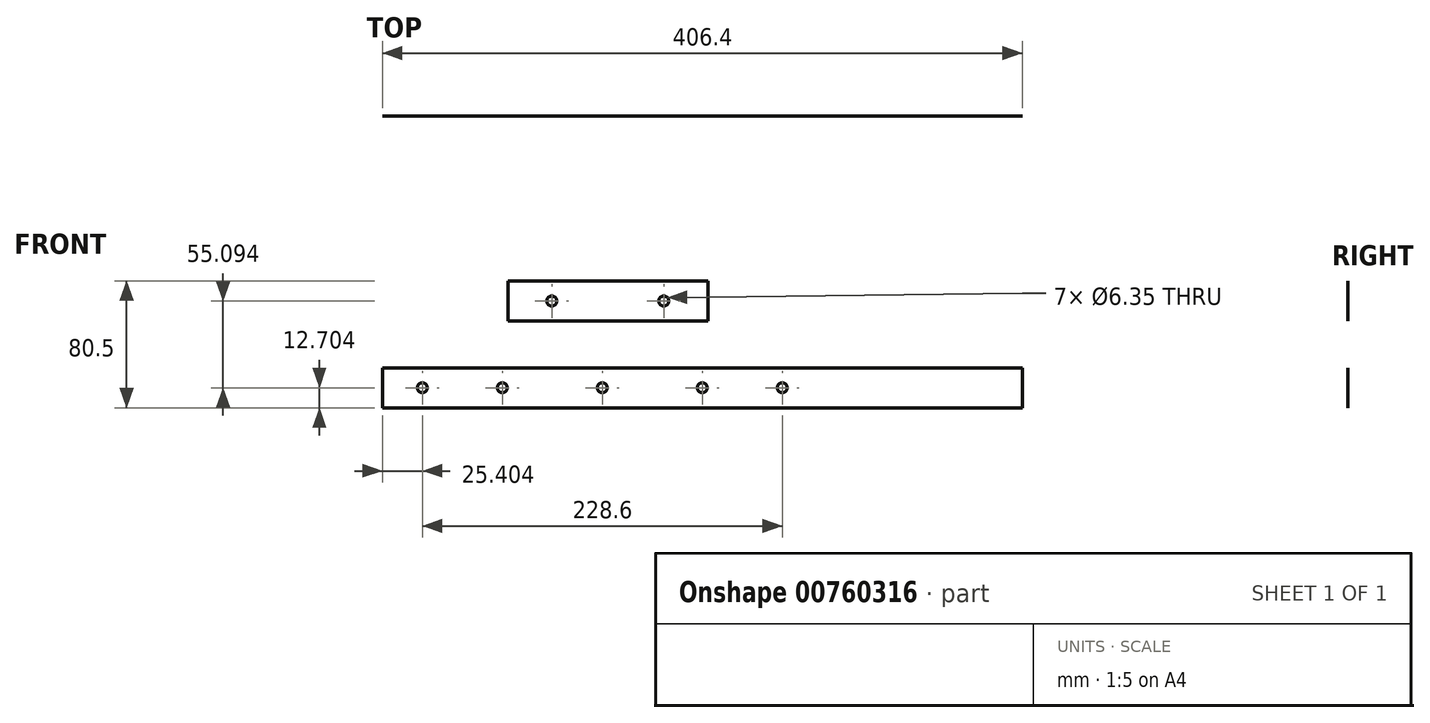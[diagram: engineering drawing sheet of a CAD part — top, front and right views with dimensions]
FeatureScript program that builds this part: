
annotation { "Feature Type Name" : "Feature", "Feature Type Description" : "" }
export const myFeature = defineFeature(function(context is Context, id is Id, definition is map)
    precondition{}
    {
        {
            var Q0;
            Q0=qCreatedBy(makeId("Front.planeOp"),FACE);
            var sketch = newSketch(context, id + "F0", { "sketchPlane" : qUnion([Q0])});
            skLineSegment(sketch, "E0.bottom", {"start": v(-178.74, 1.6) * mm, "end": v(227.66, 1.6) * mm});
            skLineSegment(sketch, "E0.top", {"start": v(-178.74, -23.8) * mm, "end": v(227.66, -23.8) * mm});
            skLineSegment(sketch, "E0.left", {"start": v(-178.74, 1.6) * mm, "end": v(-178.74, -23.8) * mm});
            skLineSegment(sketch, "E0.right", {"start": v(227.66, 1.6) * mm, "end": v(227.66, -23.8) * mm});
            skCircle(sketch, "E1", {"center": v(-153.34, -11.1) * mm, "radius": 3.18 * mm});
            skCircle(sketch, "E2", {"center": v(-102.54, -11.1) * mm, "radius": 3.18 * mm});
            skCircle(sketch, "E3", {"center": v(75.26, -11.1) * mm, "radius": 3.18 * mm});
            skCircle(sketch, "E4", {"center": v(24.46, -11.1) * mm, "radius": 3.18 * mm});
            skCircle(sketch, "E5", {"center": v(-39.04, -11.1) * mm, "radius": 3.18 * mm});
            skSolve(sketch);
        }
        {
            var Q0;
            Q0=makeQuery(id+"F0.imprint","IMPRINT",FACE,{"disambiguationData":[TD([[makeQuery(id+"F0.imprint","IMPRINT",EDGE,{"derivedFrom":sQuery(id+"F0.wireOp",EDGE,"E0.bottom")}),-1.0]])]});
            extrude(context, id + "F1", {"entities" : qUnion([Q0]), "depth" : 1 / 203.2 * mm, "offsetDistance" : 25.4 * mm});
        }
        {
            var Q0;
            Q0=qCreatedBy(makeId("Front.planeOp"),FACE);
            var sketch = newSketch(context, id + "F2", { "sketchPlane" : qUnion([Q0])});
            skLineSegment(sketch, "E6.bottom", {"start": v(-99.06, 56.7) * mm, "end": v(27.94, 56.7) * mm});
            skLineSegment(sketch, "E6.top", {"start": v(-99.06, 31.3) * mm, "end": v(27.94, 31.3) * mm});
            skLineSegment(sketch, "E6.left", {"start": v(-99.06, 56.7) * mm, "end": v(-99.06, 31.3) * mm});
            skLineSegment(sketch, "E6.right", {"start": v(27.94, 56.7) * mm, "end": v(27.94, 31.3) * mm});
            skCircle(sketch, "E7", {"center": v(-71.12, 44) * mm, "radius": 3.18 * mm});
            skCircle(sketch, "E8", {"center": v(0, 44) * mm, "radius": 3.18 * mm});
            skSolve(sketch);
        }
        {
            var Q0;
            Q0=makeQuery(id+"F2.imprint","IMPRINT",FACE,{"disambiguationData":[TD([[makeQuery(id+"F2.imprint","IMPRINT",EDGE,{"derivedFrom":sQuery(id+"F2.wireOp",EDGE,"E6.bottom")}),-1.0]])]});
            extrude(context, id + "F3", {"entities" : qUnion([Q0]), "depth" : 1 / 203.2 * mm, "offsetDistance" : 25.4 * mm});
        }
    });
